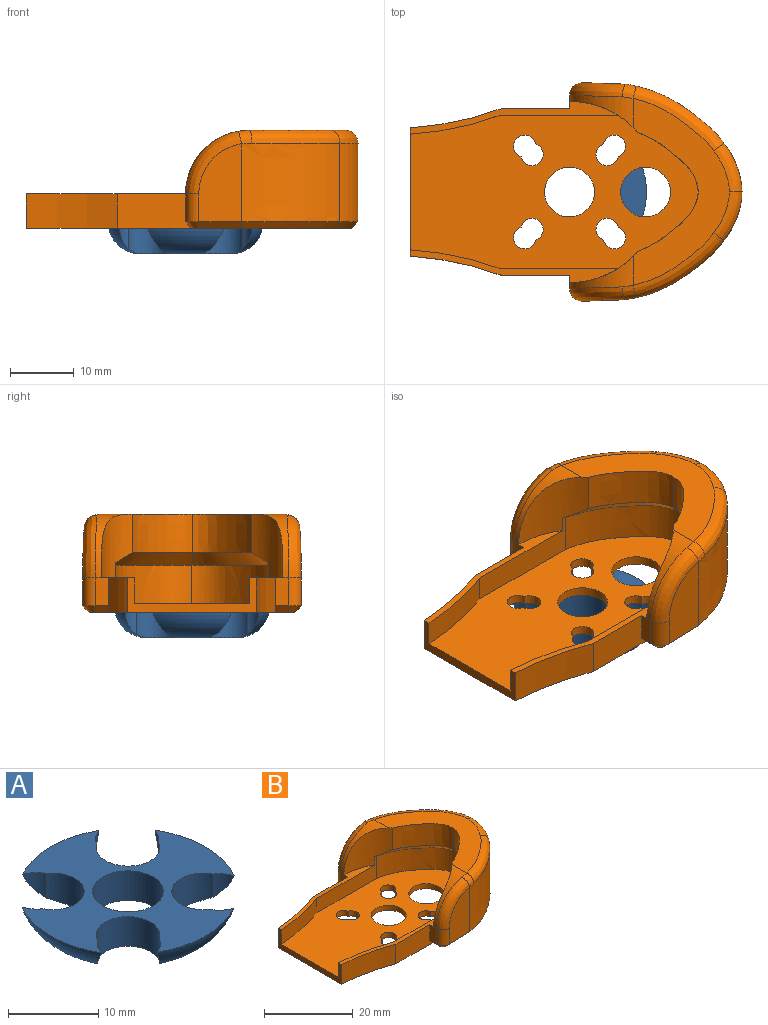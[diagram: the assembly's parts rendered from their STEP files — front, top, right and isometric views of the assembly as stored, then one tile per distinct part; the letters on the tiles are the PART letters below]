
ASSEMBLY  parts=2 mates=1
PART A: 19 faces, bbox 26.4x26.4x5 mm
  f0: plane 24.2x24.2mm, normal (0,0,1), area 236.1mm2, adj f1,f2,f3,f4,f5,f6,f7,f9
  f1: cylinder r=3.5mm len=3.15mm, axis (0,0,1), area 4.7mm2, adj f0,f14,f18
  f2: cylinder r=3.5mm len=3.36mm, axis (0,0,1), area 5.8mm2, adj f0,f14,f17
  f3: cylinder r=3.5mm len=6.61mm, axis (0,0,1), area 49.6mm2, adj f0,f8,f12,f13,f15,f16
  f4: cylinder r=3.5mm len=3.36mm, axis (0,0,1), area 5.8mm2, adj f0,f11,f17
  f5: cylinder r=3.5mm len=3.15mm, axis (0,0,1), area 4.7mm2, adj f0,f11,f16
  f6: cylinder r=3.5mm len=6.61mm, axis (0,0,1), area 49.6mm2, adj f0,f8,f9,f10,f15,f18
  f7: cylinder r=3.92mm len=7.85mm, axis (0,0,1), area 98.6mm2, adj f0,f8
  f8: plane 14.4x14.4mm, normal (0,0,-1), area 75mm2, adj f3,f6,f7,f11,f14,f15,f16,f17
  f9: cylinder r=3.5mm len=3.36mm, axis (0,0,1), area 5.8mm2, adj f0,f6,f15
  f10: cylinder r=3.5mm len=3.15mm, axis (0,0,1), area 4.7mm2, adj f0,f6,f18
  f11: cylinder r=3.5mm len=6.61mm, axis (0,0,1), area 49.6mm2, adj f0,f4,f5,f8,f16,f17
  f12: cylinder r=3.5mm len=3.15mm, axis (0,0,1), area 4.7mm2, adj f0,f3,f16
  f13: cylinder r=3.5mm len=3.36mm, axis (0,0,1), area 5.8mm2, adj f0,f3,f15
  f14: cylinder r=3.5mm len=6.61mm, axis (0,0,1), area 49.6mm2, adj f0,f1,f2,f8,f17,f18
  f15: torus R=7.2mm, axis (0,0,-1), area 60.8mm2, adj f0,f3,f6,f8,f9,f13
  f16: torus R=7.2mm, axis (0,0,-1), area 62.7mm2, adj f0,f3,f5,f8,f11,f12
  f17: torus R=7.2mm, axis (0,0,-1), area 60.8mm2, adj f0,f2,f4,f8,f11,f14
  f18: torus R=7.2mm, axis (0,0,-1), area 62.7mm2, adj f0,f1,f6,f8,f10,f14
PART B: 62 faces, bbox 52.6x34.7x15.8 mm
  f0: cylinder r=14.25mm len=10.72mm, axis (0,0,-1), area 86mm2, adj f1,f17,f35,f37,f38,f51
  f1: plane 32.65x5.18mm, normal (0,0,1), area 36.1mm2, adj f0,f2,f9,f17,f22,f23,f26
  f2: plane 11.78x5.4mm, normal (0,-1,0), area 58.7mm2, adj f1,f16,f23,f26,f52
  f3: plane 11.78x5.4mm, normal (0,1,0), area 58.7mm2, adj f16,f24,f25,f33,f61
  f4: cylinder r=1.75mm len=3.46mm, axis (0,0,-1), area 10.3mm2, adj f14,f15,f16
  f5: cylinder r=1.75mm len=3.46mm, axis (0,0,-1), area 10.3mm2, adj f8,f15,f16
  f6: cylinder r=1.75mm len=3.46mm, axis (0,0,-1), area 10.3mm2, adj f10,f15,f16
  f7: cylinder r=1.75mm len=3.46mm, axis (0,0,-1), area 10.3mm2, adj f11,f15,f16
  f8: cylinder r=1.75mm len=3.46mm, axis (0,0,-1), area 10.3mm2, adj f5,f15,f16
  f9: plane 20.18x5.4mm, normal (-1,0,0), area 36.3mm2, adj f1,f15,f16,f21,f22,f23,f24,f25
  f10: cylinder r=1.75mm len=3.46mm, axis (0,0,-1), area 10.3mm2, adj f6,f15,f16
  f11: cylinder r=1.75mm len=3.46mm, axis (0,0,-1), area 10.3mm2, adj f7,f15,f16
  f12: cylinder r=3.92mm len=7.85mm, axis (0,0,-1), area 34.5mm2, adj f15,f16
  f13: cylinder r=3.92mm len=7.85mm, axis (0,0,-1), area 34.5mm2, adj f15,f16
  f14: cylinder r=1.75mm len=3.46mm, axis (0,0,-1), area 10.3mm2, adj f4,f15,f16
  f15: plane 47.33x24.2mm, normal (0,0,1), area 835.4mm2, adj f4,f5,f6,f7,f8,f9,f10,f11
  f16: plane 51.58x32.7mm, normal (0,0,-1), area 1121.9mm2, adj f2,f3,f4,f5,f6,f7,f8,f9
  f17: plane 19x6.37mm, normal (0,1,0), area 77.6mm2, adj f0,f1,f15,f18,f22,f51
  f18: extruded ~14x12.1mm, area 120mm2, adj f15,f17,f19,f51
  f19: extruded ~14x12.1mm, area 120mm2, adj f15,f18,f20,f50
  f20: plane 19x6.37mm, normal (0,-1,0), area 77.6mm2, adj f15,f19,f21,f25,f34,f50
  f21: cylinder r=50mm len=14.33mm, axis (0,0,-1), area 58.8mm2, adj f9,f15,f20,f25
  f22: cylinder r=50mm len=14.33mm, axis (0,0,-1), area 58.8mm2, adj f1,f9,f15,f17
  f23: cylinder r=50mm len=14.33mm, axis (0,0,-1), area 79.3mm2, adj f1,f2,f9,f16
  f24: cylinder r=50mm len=14.33mm, axis (0,0,-1), area 79.3mm2, adj f3,f9,f16,f25
  f25: plane 32.65x5.18mm, normal (0,0,1), area 36.1mm2, adj f3,f9,f20,f21,f24,f33,f34
  f26: plane 4.4x2.08mm, normal (-1,0,0), area 9.2mm2, adj f1,f2,f38,f42,f52
  f27: plane 12.3x6.74mm, normal (0.03,-1,0), area 69.7mm2, adj f28,f42,f44,f46,f54
  f28: extruded ~15.49x12.4mm, area 229.3mm2, adj f27,f29,f46,f48,f55
  f29: extruded ~12.4x7.64mm, area 102.8mm2, adj f28,f30,f49,f56
  f30: extruded ~12.4x7.64mm, area 102.8mm2, adj f29,f31,f47,f57
  f31: extruded ~15.49x12.4mm, area 229.3mm2, adj f30,f32,f43,f45,f57,f58
  f32: plane 12.3x6.75mm, normal (0.03,1,0), area 69.7mm2, adj f31,f40,f41,f43,f59
  f33: plane 4.4x2.08mm, normal (-1,0,0), area 9.2mm2, adj f3,f25,f39,f40,f61
  f34: cylinder r=14.25mm len=10.72mm, axis (0,0,-1), area 86mm2, adj f20,f25,f35,f36,f39,f50
  f35: plane 29.39x15.13mm, normal (0,0,1), area 180.4mm2, adj f0,f34,f36,f37,f38,f39,f45,f47
  f36: extruded ~9.51x9.39mm, area 84mm2, adj f34,f35,f37,f50
  f37: extruded ~9.51x9.39mm, area 84mm2, adj f0,f35,f36,f51
  f38: cylinder r=10mm len=10mm, axis (0,1,0), area 26mm2, adj f0,f26,f35,f44,f46
  f39: cylinder r=10mm len=10mm, axis (0,1,0), area 26mm2, adj f33,f34,f35,f41,f43
  f40: cylinder r=2mm len=4.4mm, axis (0,0,-1), area 14.1mm2, adj f32,f33,f41,f60
  f41: bspline ~9.87x8.79mm, area 41.6mm2, adj f32,f39,f40,f43
  f42: cylinder r=2mm len=4.4mm, axis (0,0,-1), area 14.1mm2, adj f26,f27,f44,f53
  f43: bspline ~3.18x2.45mm, area 5.7mm2, adj f31,f32,f39,f41,f45
  f44: bspline ~9.87x8.79mm, area 41.6mm2, adj f27,f38,f42,f46
  f45: bspline ~17.44x13.58mm, area 51.3mm2, adj f31,f35,f43,f47
  f46: bspline ~3.18x2.45mm, area 5.7mm2, adj f27,f28,f38,f44,f48
  f47: bspline ~8.15x4.64mm, area 24.7mm2, adj f30,f35,f45,f49
  f48: bspline ~16.05x11.78mm, area 51.3mm2, adj f28,f35,f46,f49
  f49: bspline ~8.2x4.63mm, area 24.6mm2, adj f29,f35,f47,f48
  f50: bspline ~16.9x14.73mm, area 49mm2, adj f19,f20,f34,f36,f51
  f51: bspline ~14.9x12.5mm, area 49mm2, adj f0,f17,f18,f37,f50
  f52: plane 2.08x1mm, normal (-0.71,0,-0.71), area 2.9mm2, adj f2,f16,f26,f53
  f53: cone r=1mm half-angle=45deg, axis (0,0,1), area 3.4mm2, adj f16,f42,f52,f54
  f54: plane 6.78x1.23mm, normal (0.02,-0.71,-0.71), area 9.5mm2, adj f16,f27,f53,f55
  f55: bspline ~17.05x10.78mm, area 25.5mm2, adj f16,f28,f54,f56
  f56: bspline ~7.69x3.64mm, area 11.3mm2, adj f16,f29,f55,f57
  f57: bspline ~8.39x3.9mm, area 11.4mm2, adj f16,f30,f31,f56,f58
  f58: bspline ~17.04x10.78mm, area 25.5mm2, adj f16,f31,f57,f59
  f59: plane 6.78x1.24mm, normal (0.02,0.71,-0.71), area 9.5mm2, adj f16,f32,f58,f60
  f60: cone r=1mm half-angle=45deg, axis (0,0,1), area 3.4mm2, adj f16,f40,f59,f61
  f61: plane 2.08x1mm, normal (-0.71,0,-0.71), area 2.9mm2, adj f3,f16,f33,f60
PLACE A at identity
PLACE B t=(8.23,0,0)mm
MATE fastened B.f0 <-> A.f7  axis (0,0,1) through (0,0,0)mm
